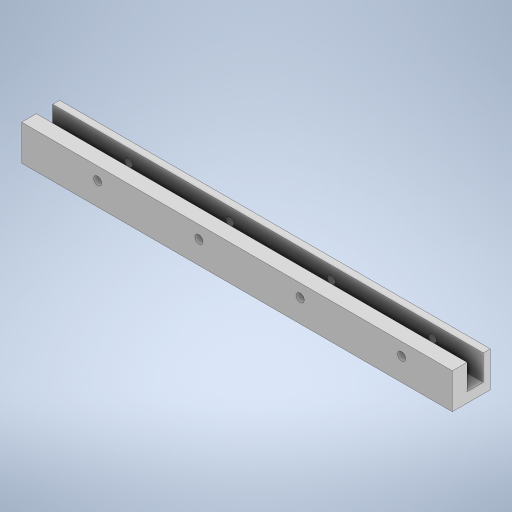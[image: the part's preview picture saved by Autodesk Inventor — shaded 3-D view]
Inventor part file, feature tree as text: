
AUTODESK INVENTOR PART (.ipt)
format: ipt  version: 2023 (Build 270158000, 158)  size: 300,032 bytes
history: native  units: mm
features: sketch x7, extrude x5, hole x2, other x1
ambient origin geometry x8: Origin, YZ Plane, XZ Plane, XY Plane, X Axis, Y Axis, Z Axis, Center Point
bodies: Body1 (feature_tree)
feature tree (15):
  other  "ソリッド1"
  extrude  "押し出し1"  Depth=180.0mm
  extrude  "押し出し2"  Depth=6.0mm
  extrude  "押し出し3"  Depth=17.0mm TaperAngle=0.0deg
  extrude  "押し出し4"  Depth=170.0mm
  extrude  "押し出し5"  Depth=6.0mm
  hole  "穴1"  [1 undecoded]
  hole  "穴2"  [1 undecoded]
  sketch  "スケッチ1"
  sketch  "スケッチ2"
  sketch  "スケッチ3"
  sketch  "スケッチ4"
  sketch  "スケッチ5"
  sketch  "スケッチ6"
  sketch  "スケッチ7"
note: 2 required parameter values undecoded (feature->parameter linkage not recoverable at this tier; creation-order binding heuristic only, values carry confidence <= 0.55)
